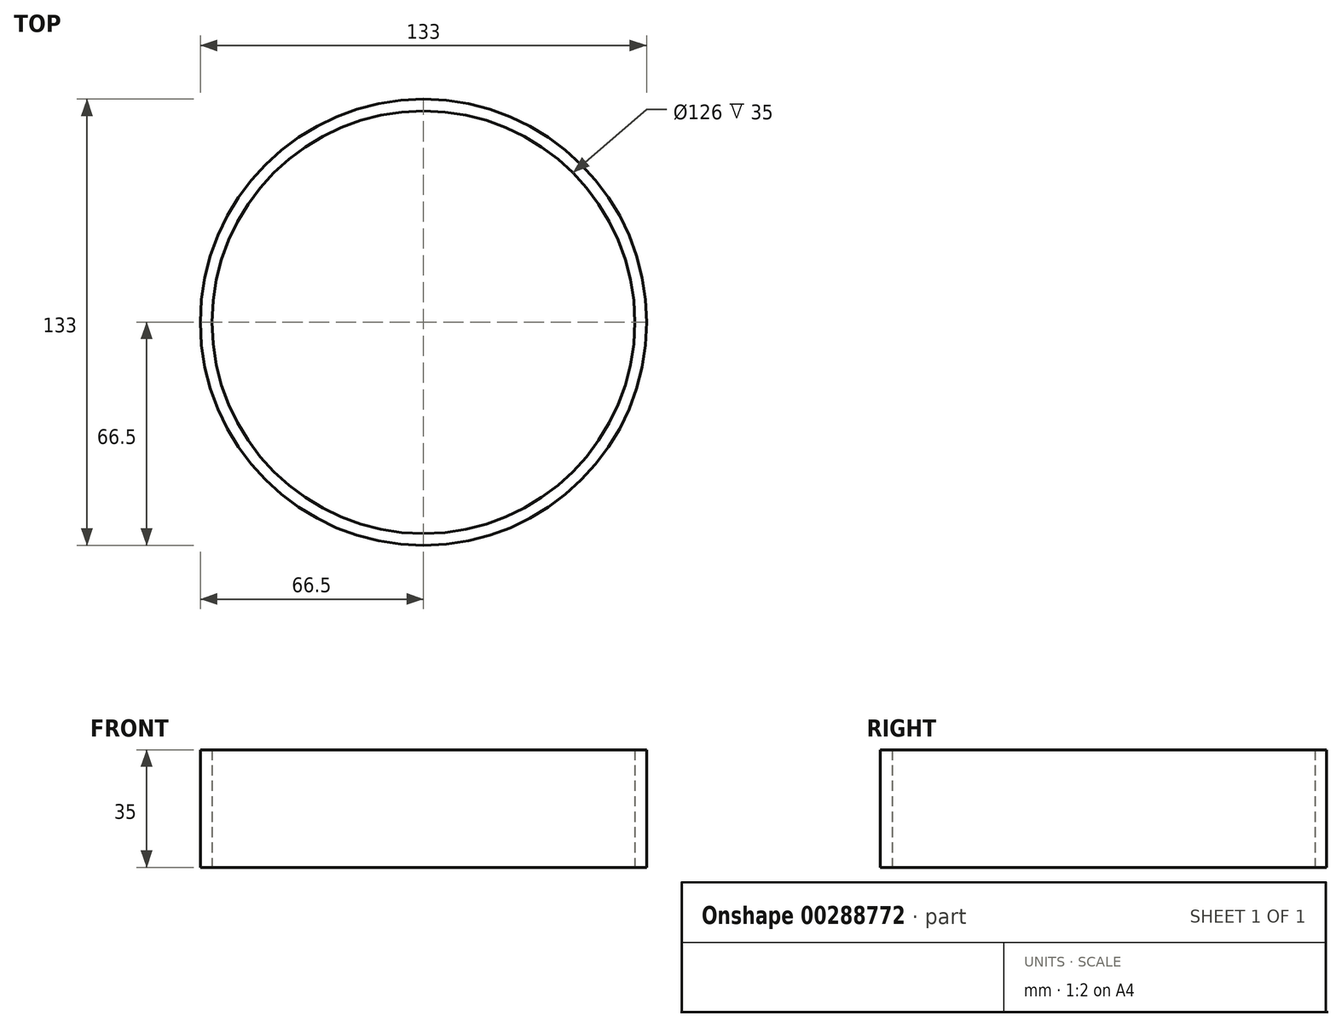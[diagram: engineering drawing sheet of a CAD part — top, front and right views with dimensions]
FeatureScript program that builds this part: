
annotation { "Feature Type Name" : "Feature", "Feature Type Description" : "" }
export const myFeature = defineFeature(function(context is Context, id is Id, definition is map)
    precondition{}
    {
        {
            var Q0;
            Q0=qCreatedBy(makeId("Top.planeOp"),FACE);
            var sketch = newSketch(context, id + "F0", { "sketchPlane" : qUnion([Q0])});
            skCircle(sketch, "E0", {"center": v(0, 0) * mm, "radius": 66.5 * mm});
            skCircle(sketch, "E1.0", {"center": v(0, 0) * mm, "radius": 63 * mm});
            skSolve(sketch);
        }
        {
            var Q0;
            Q0 = qSketchRegion(id + "F0", true);
            extrude(context, id + "F1", {"entities" : qUnion([Q0]), "depth" : 35 * mm});
        }
    });
